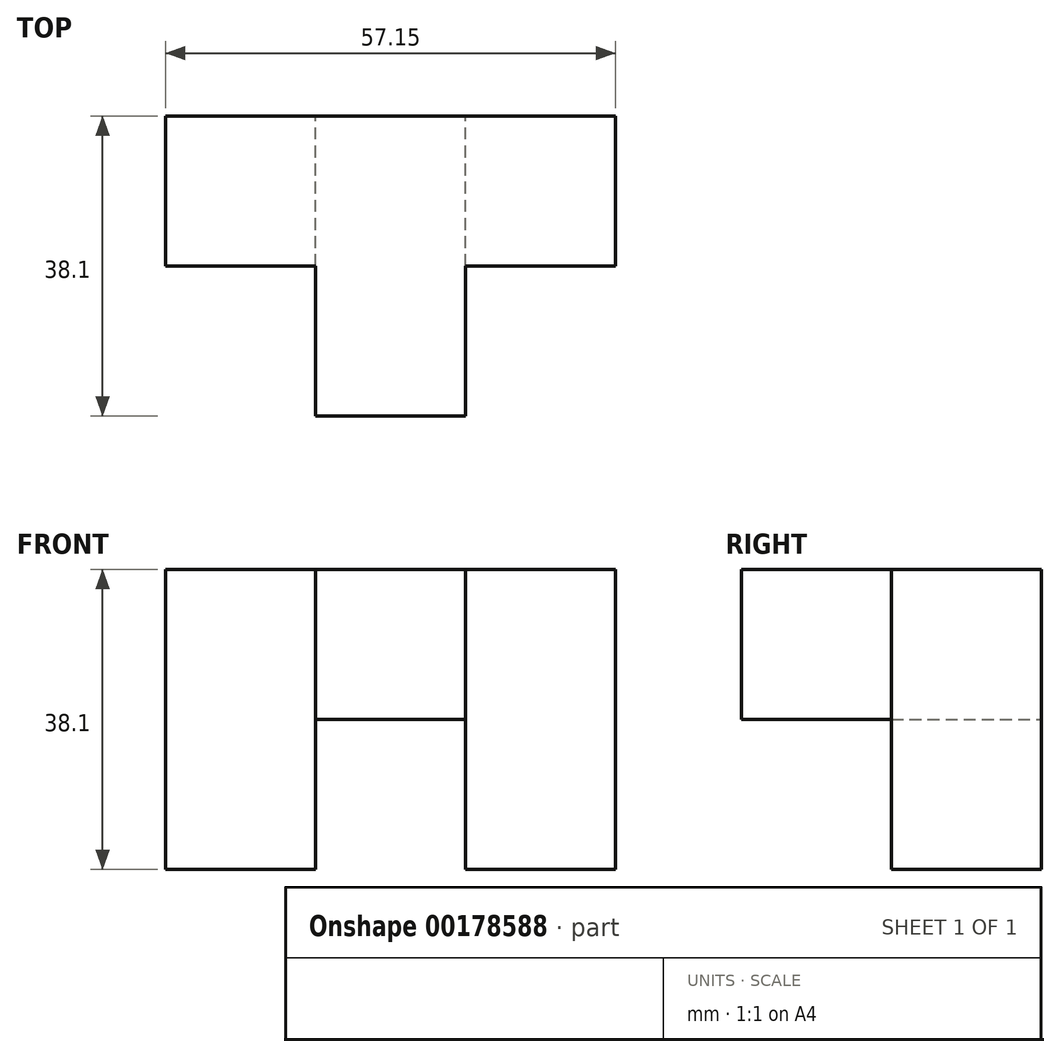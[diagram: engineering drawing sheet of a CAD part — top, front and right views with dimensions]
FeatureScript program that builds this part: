
annotation { "Feature Type Name" : "Feature", "Feature Type Description" : "" }
export const myFeature = defineFeature(function(context is Context, id is Id, definition is map)
    precondition{}
    {
        {
            var Q0;
            Q0=qCreatedBy(makeId("Front.planeOp"),FACE);
            var sketch = newSketch(context, id + "F0", { "sketchPlane" : qUnion([Q0])});
            skLineSegment(sketch, "E0", {"start": v(-57.35, 48.62) * mm, "end": v(-57.35, 29.57) * mm});
            skLineSegment(sketch, "E1", {"start": v(-57.35, 29.57) * mm, "end": v(-38.3, 29.57) * mm});
            skLineSegment(sketch, "E2", {"start": v(-38.3, 29.57) * mm, "end": v(-38.3, 48.62) * mm});
            skLineSegment(sketch, "E3", {"start": v(-38.3, 48.62) * mm, "end": v(-57.35, 48.62) * mm});
            skLineSegment(sketch, "E4", {"start": v(-57.35, 29.57) * mm, "end": v(-57.35, 10.52) * mm});
            skLineSegment(sketch, "E5", {"start": v(-38.3, 10.52) * mm, "end": v(-38.3, 29.57) * mm});
            skLineSegment(sketch, "E6", {"start": v(-38.3, 10.52) * mm, "end": v(-57.35, 10.52) * mm});
            skLineSegment(sketch, "E7", {"start": v(-38.3, 48.62) * mm, "end": v(-19.25, 48.62) * mm});
            skLineSegment(sketch, "E8", {"start": v(-19.25, 48.62) * mm, "end": v(-19.25, 29.57) * mm});
            skLineSegment(sketch, "E9", {"start": v(-38.3, 29.57) * mm, "end": v(-19.25, 29.57) * mm});
            skLineSegment(sketch, "E10", {"start": v(-0.2, 29.57) * mm, "end": v(-0.2, 48.62) * mm});
            skLineSegment(sketch, "E11", {"start": v(-0.2, 48.62) * mm, "end": v(-19.25, 48.62) * mm});
            skLineSegment(sketch, "E12", {"start": v(-19.25, 29.57) * mm, "end": v(-0.2, 29.57) * mm});
            skLineSegment(sketch, "E13", {"start": v(-19.25, 29.57) * mm, "end": v(-19.25, 10.52) * mm});
            skLineSegment(sketch, "E14", {"start": v(-19.25, 10.52) * mm, "end": v(-0.2, 10.52) * mm});
            skLineSegment(sketch, "E15", {"start": v(-0.2, 10.52) * mm, "end": v(-0.2, 29.57) * mm});
            skSolve(sketch);
        }
        {
            var Q0;
            Q0 = qSketchRegion(id + "F0", true);
            extrude(context, id + "F1", {"entities" : qUnion([Q0]), "depth" : 19.05 * mm});
        }
        {
            var Q0;
            Q0=makeQuery(id+"F1.opExtrude","CAP_FACE",FACE,{"disambiguationData":[OSD([sQuery(id+"F0.wireOp",EDGE,"E0"),sQuery(id+"F0.wireOp",EDGE,"E3"),sQuery(id+"F0.wireOp",EDGE,"E4"),sQuery(id+"F0.wireOp",EDGE,"E5"),sQuery(id+"F0.wireOp",EDGE,"E6"),sQuery(id+"F0.wireOp",EDGE,"E7"),sQuery(id+"F0.wireOp",EDGE,"E9"),sQuery(id+"F0.wireOp",EDGE,"E10"),sQuery(id+"F0.wireOp",EDGE,"E11"),sQuery(id+"F0.wireOp",EDGE,"E13"),sQuery(id+"F0.wireOp",EDGE,"E14"),sQuery(id+"F0.wireOp",EDGE,"E15")])],"isStart":false});
            var sketch = newSketch(context, id + "F2", { "sketchPlane" : qUnion([Q0])});
            skLineSegment(sketch, "E16", {"start": v(-38.3, 29.57) * mm, "end": v(-38.3, 48.62) * mm});
            skLineSegment(sketch, "E17", {"start": v(-38.3, 48.62) * mm, "end": v(-19.25, 48.62) * mm});
            skLineSegment(sketch, "E18", {"start": v(-19.25, 48.62) * mm, "end": v(-19.25, 29.57) * mm});
            skLineSegment(sketch, "E19", {"start": v(-19.25, 29.57) * mm, "end": v(-38.3, 29.57) * mm});
            skSolve(sketch);
        }
        {
            var Q0;
            Q0 = qSketchRegion(id + "F2", true);
            extrude(context, id + "F3", {"entities" : qUnion([Q0]), "operationType" : NewBodyOperationType.ADD, "depth" : 19.05 * mm});
        }
    });
